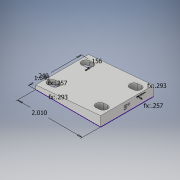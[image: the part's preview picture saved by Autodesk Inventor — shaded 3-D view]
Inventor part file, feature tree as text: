
AUTODESK INVENTOR PART (.ipt)
format: ipt  version: 2018 (Build 220112000, 112)  size: 203,776 bytes
history: native  units: in
note: dims shown in document units (in); Inventor stores cm internally (conversion verified against a paired STEP export)
features: sketch x4, extrude x3, projected_geometry x1
ambient origin geometry x8: Origin, YZ Plane, XZ Plane, XY Plane, X Axis, Y Axis, Z Axis, Center Point
bodies: Body1 (feature_tree)
feature tree (8):
  sketch  "Sketch1"  dims[d0=0.1562in d1=1.64in]
  extrude  "Extrusion8"  Depth=1.64in
  extrude  "Extrusion9"  Depth=0.24in
  extrude  "Extrusion10"  Depth=0.257in
  sketch  "Sketch10"  dims[d2=2.01in d3=0.24in]
  sketch  "Sketch11"  dims[d4=0.293in d5=0.257in]
  sketch  "Sketch13"  dims[d6=0.293in d7=0.257in d20=0.125in d21=1.25in d22=0.125in d23=0.125in d24=0.1875in d25=0.0938in d61=0.0344in d62=0.125in d63=1.64in d64=0.0in d65=0.125in d66=0.12in d67=1.64in d68=0.0in d69=0.08in d70=0.015in d71=0.0in]
  projected_geometry  "Projected Loop1"
